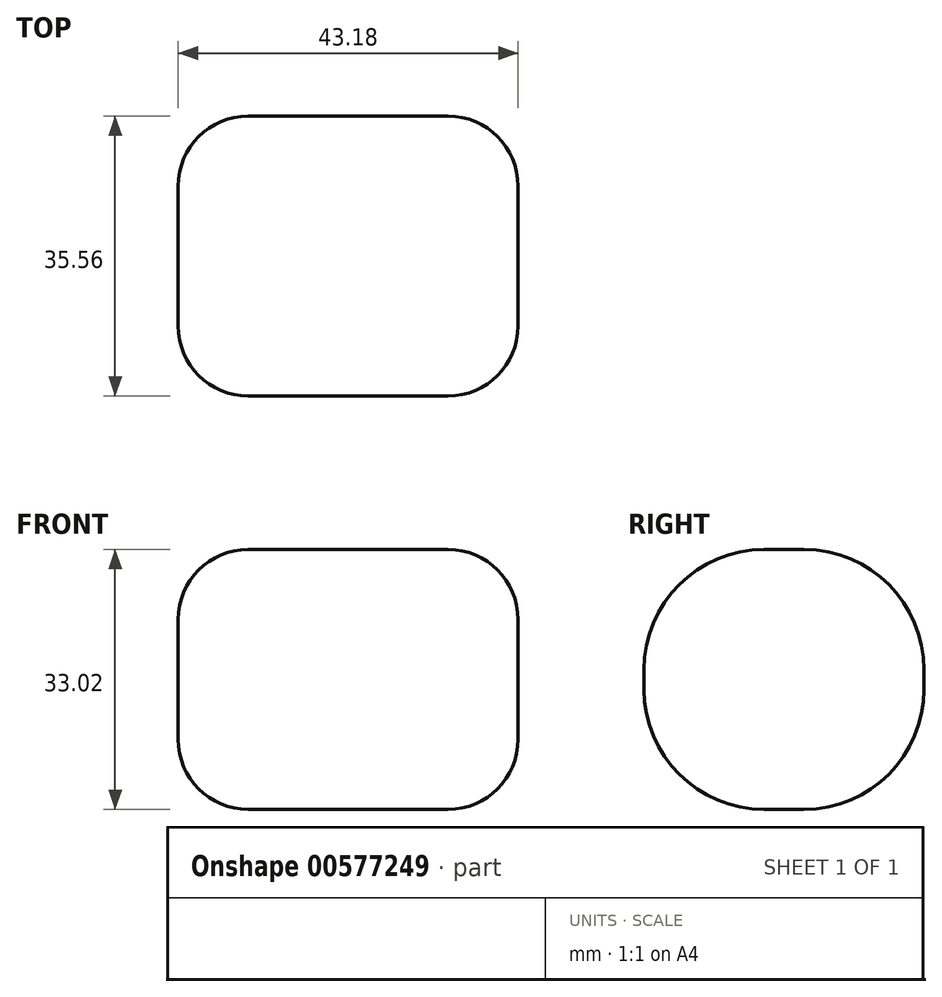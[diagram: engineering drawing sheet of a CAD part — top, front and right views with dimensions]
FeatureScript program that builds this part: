
annotation { "Feature Type Name" : "Feature", "Feature Type Description" : "" }
export const myFeature = defineFeature(function(context is Context, id is Id, definition is map)
    precondition{}
    {
        {
            var Q0;
            Q0=qCreatedBy(makeId("Front.planeOp"),FACE);
            var sketch = newSketch(context, id + "F0", { "sketchPlane" : qUnion([Q0])});
            skLineSegment(sketch, "E0.bottom", {"start": v(21.59, -16.51) * mm, "end": v(-21.6, -16.51) * mm});
            skLineSegment(sketch, "E0.top", {"start": v(21.59, 16.51) * mm, "end": v(-21.59, 16.51) * mm});
            skLineSegment(sketch, "E0.left", {"start": v(21.59, -16.5) * mm, "end": v(21.59, 16.51) * mm});
            skLineSegment(sketch, "E0.right", {"start": v(-21.6, -16.51) * mm, "end": v(-21.6, 16.51) * mm});
            skPoint(sketch, "E0.middle", {"position": v(0, 0) * mm});
            skSolve(sketch);
        }
        {
            var Q0;
            Q0=makeQuery(id+"F0.imprint","IMPRINT",FACE,{"disambiguationData":[TD([[makeQuery(id+"F0.imprint","IMPRINT",EDGE,{"derivedFrom":sQuery(id+"F0.wireOp",EDGE,"E0.bottom")}),-1.0]])]});
            extrude(context, id + "F1", {"entities" : qUnion([Q0]), "endBound" : BoundingType.SYMMETRIC, "depth" : 35.56 * mm, "offsetDistance" : 25.4 * mm});
        }
        {
            var Q0;
            Q0=makeQuery(id+"F1.opExtrude","CAP_EDGE",EDGE,{"disambiguationData":[OSD([sQuery(id+"F0.wireOp",EDGE,"E0.top")])],"isStart":false});
            fillet(context, id + "F2", {"entities" : qUnion([Q0]), "radius" : 15.24 * mm, "tangentPropagation" : true, "allowEdgeOverflow" : false});
        }
        {
            var Q0;
            Q0=makeQuery(id+"F1.opExtrude","CAP_EDGE",EDGE,{"disambiguationData":[OSD([sQuery(id+"F0.wireOp",EDGE,"E0.bottom")])],"isStart":false});
            var Q1;
            Q1=makeQuery(id+"F1.opExtrude","CAP_EDGE",EDGE,{"disambiguationData":[OSD([sQuery(id+"F0.wireOp",EDGE,"E0.bottom")])],"isStart":true});
            var Q2;
            Q2=makeQuery(id+"F1.opExtrude","CAP_EDGE",EDGE,{"disambiguationData":[OSD([sQuery(id+"F0.wireOp",EDGE,"E0.top")])],"isStart":true});
            fillet(context, id + "F3", {"entities" : qUnion([Q0, Q1, Q2]), "radius" : 15.24 * mm, "tangentPropagation" : true, "allowEdgeOverflow" : false});
        }
        {
            var Q0;
            Q0=makeQuery(id+"F2.opFillet","BLEND_EDGE",EDGE,{"blendedFrom":[makeQuery(id+"F1.opExtrude","CAP_EDGE",EDGE,{"disambiguationData":[OSD([sQuery(id+"F0.wireOp",EDGE,"E0.top")])],"isStart":false}),makeQuery(id+"F1.opExtrude","SWEPT_FACE",FACE,{"disambiguationData":[OSD([sQuery(id+"F0.wireOp",EDGE,"E0.left")])]})],"blendedInto":[makeQuery(id+"F1.opExtrude","SWEPT_FACE",FACE,{"disambiguationData":[OSD([sQuery(id+"F0.wireOp",EDGE,"E0.left")])]})]});
            var Q1;
            Q1=makeQuery(id+"F3.opFillet","BLEND_EDGE",EDGE,{"blendedFrom":[makeQuery(id+"F1.opExtrude","CAP_EDGE",EDGE,{"disambiguationData":[OSD([sQuery(id+"F0.wireOp",EDGE,"E0.bottom")])],"isStart":false}),makeQuery(id+"F1.opExtrude","SWEPT_FACE",FACE,{"disambiguationData":[OSD([sQuery(id+"F0.wireOp",EDGE,"E0.right")])]})],"blendedInto":[makeQuery(id+"F1.opExtrude","SWEPT_FACE",FACE,{"disambiguationData":[OSD([sQuery(id+"F0.wireOp",EDGE,"E0.right")])]})]});
            fillet(context, id + "F4", {"entities" : qUnion([Q0, Q1]), "radius" : 8.9 * mm, "tangentPropagation" : true, "allowEdgeOverflow" : false});
        }
    });
